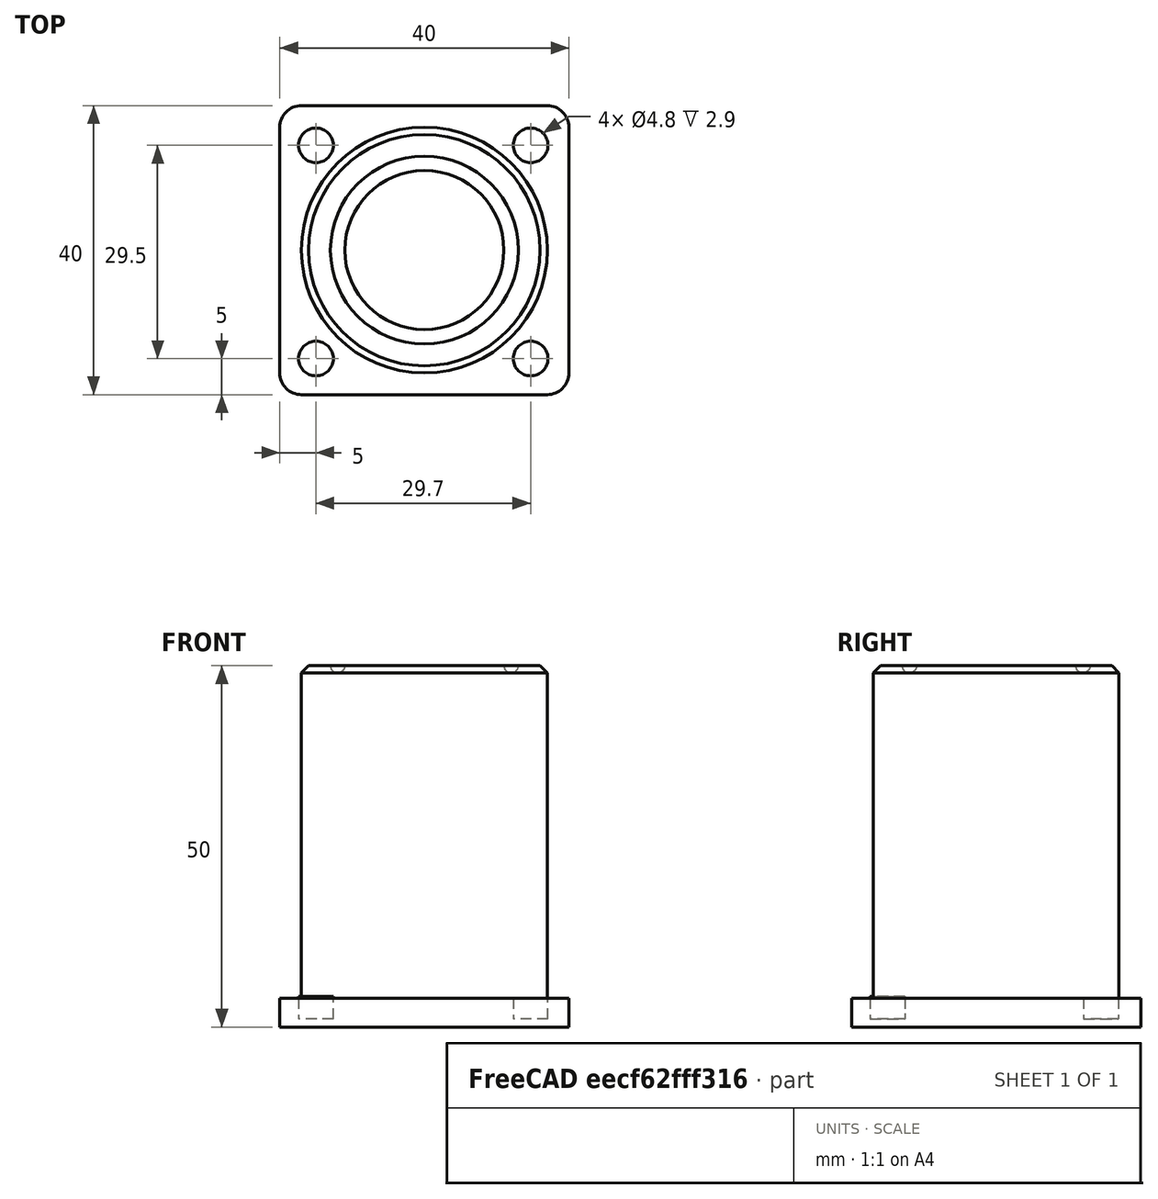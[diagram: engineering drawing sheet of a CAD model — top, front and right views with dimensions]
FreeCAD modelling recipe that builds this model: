
FCSTD DOCUMENT  (FreeCAD 0.21R33694 (Git))
Label: OJT1_T15R03_pota_taula
License: All rights reserved
LicenseURL: https://en.wikipedia.org/wiki/All_rights_reserved
objects: Part::Fillet×4, Part::Cylinder×2, Part::Cut×2, Part::Box×1, Part::FeaturePython×1, Part::Torus×1, Part::Chamfer×1, Part::MultiFuse×1
note: 12 computed .brp shape members not serialized (recipe doc carries the construction recipe); baked Part::Feature solids carry a one-line shape summary decoded from their .brp

FEATURE [Part::Box] Box  label="Base"
  AttacherType = Attacher::AttachEngine3D
  Height = 4
  Length = 40
  Width = 40
FEATURE [Part::Fillet] Fillet
  Base = -> Box
  Edges = 1 edges r=3: [Edge1]
FEATURE [Part::Fillet] Fillet001
  Base = -> Fillet
  Edges = 1 edges r=3: [Edge15]
FEATURE [Part::Fillet] Fillet002
  Base = -> Fillet001
  Edges = 1 edges r=3: [Edge15]
FEATURE [Part::Fillet] Fillet003
  Base = -> Fillet002
  Edges = 1 edges r=3: [Edge16]
FEATURE [Part::Cylinder] Cylinder  label="Cilindre"
  Angle = 360
  AttacherType = Attacher::AttachEngine3D
  FirstAngle = 0
  Height = 3.1
  Placement = pos=(5,5,1.1) rot=(0,0,1;0rad)
  Radius = 2.4
  SecondAngle = 0
FEATURE [Part::FeaturePython] Array  # Draft array (typed FeaturePython)
  AlwaysSyncPlacement = false
  Angle = 360
  ArrayType = 0
  Axis = (0,0,1)
  Base = -> Cylinder
  Center = (0,0,0)
  Count = 4
  ExpandArray = false
  Fuse = false
  IntervalAxis = (0,0,0)
  IntervalX = (29.7,0,0)
  IntervalY = (0,29.5,0)
  IntervalZ = (0,0,100)
  NumberCircles = 3
  NumberPolar = 5
  NumberX = 2
  NumberY = 2
  NumberZ = 1
  PlacementList = 4 placements: [(5,5,1.1),(5,34.5,1.1),(34.7,5,1.1),(34.7,34.5,1.1)]
  RadialDistance = 50
  ScaleList = (4) [(1,1,1),(1,1,1),(1,1,1),(1,1,1)]
  Symmetry = 1
  TangentialDistance = 25
FEATURE [Part::Cut] Cut
  Base = -> Fillet003
  Tool = -> Array
FEATURE [Part::Cylinder] Cylinder001  label="Clindre_gran"
  Angle = 360
  AttacherType = Attacher::AttachEngine3D
  FirstAngle = 0
  Height = 50
  Placement = pos=(20,20,0) rot=(0,0,1;0rad)
  Radius = 17
  SecondAngle = 0
FEATURE [Part::Torus] Torus
  Angle1 = -180
  Angle2 = 180
  Angle3 = 360
  AttacherType = Attacher::AttachEngine3D
  Placement = pos=(20,20,50) rot=(0,0,1;0rad)
  Radius1 = 12
  Radius2 = 1
FEATURE [Part::Chamfer] Chamfer
  Base = -> Cylinder001
  Edges = 1 edges r=1: [Edge3]
FEATURE [Part::MultiFuse] Fusion
  Shapes = -> [Cut,Chamfer]
FEATURE [Part::Cut] Cut001
  Base = -> Fusion
  Tool = -> Torus
